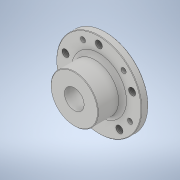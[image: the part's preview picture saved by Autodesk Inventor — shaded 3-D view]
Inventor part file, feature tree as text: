
AUTODESK INVENTOR PART (.ipt)
format: ipt  version: 2021 (Build 250183000, 183)  size: 215,040 bytes
history: native  units: in
note: dims shown in document units (in); Inventor stores cm internally (conversion verified against a paired STEP export)
features: thread x6, sketch x6, extrude x5, fillet x2, revolve x1, chamfer x1
ambient origin geometry x8: Origin, YZ Plane, XZ Plane, XY Plane, X Axis, Y Axis, Z Axis, Center Point
bodies: Solid1 (feature_tree)
feature tree (21):
  revolve  "Revolution1"  [1 undecoded]
  extrude  "Extrusion1"  Depth=0.435in
  extrude  "Extrusion2"  Depth=0.2in
  fillet  "Fillet1"  Radius=0.16in
  chamfer  "Chamfer1"  Distance=1.0in
  fillet  "Fillet2"  Radius=1.25in
  extrude  "Extrusion3"  Depth=0.435in TaperAngle=0.0deg
  thread  "Thread1"  [1 undecoded]
  thread  "Thread2"  [1 undecoded]
  thread  "Thread3"  [1 undecoded]
  thread  "Thread4"  [1 undecoded]
  thread  "Thread5"  [1 undecoded]
  thread  "Thread6"  [1 undecoded]
  extrude  "Extrusion4"  TaperAngle=45.0deg  [1 undecoded]
  extrude  "Extrusion5"  Depth=0.435in
  sketch  "Sketch1"  dims[d0=1.5in d1=1.56in]
  sketch  "Sketch2"  dims[d2=1.2in d3=0.435in]
  sketch  "Sketch3"  dims[d4=1.42in d5=0.2in d6=0.16in]
  sketch  "Sketch4"  dims[d7=0.52in]
  sketch  "Sketch5"  dims[d8=90.0deg]
  sketch  "Sketch6"  dims[d9=2.0in d10=1.0in d11=0.0in d12=1.25in d13=1.0in d14=0.0in d15=0.075in d16=0.03in d17=0.125in d18=45.0deg d19=0.25in d20=0.452in d21=0.48in d22=1.9685in d24=360.0deg d26=45.0deg d27=0.2in d28=0.2in d29=0.0in d30=0.435in d31=0.0in d32=0.435in d33=0.0in d34=0.435in d35=0.0in d36=0.435in d37=0.0in d38=0.435in d39=0.0in d40=0.435in d41=0.0in d42=1.0in d43=0.0in d44=0.325in d45=1.9685in d47=360.0deg d49=1.0in d50=0.0in]
note: 8 required parameter values undecoded (feature->parameter linkage not recoverable at this tier; creation-order binding heuristic only, values carry confidence <= 0.55)